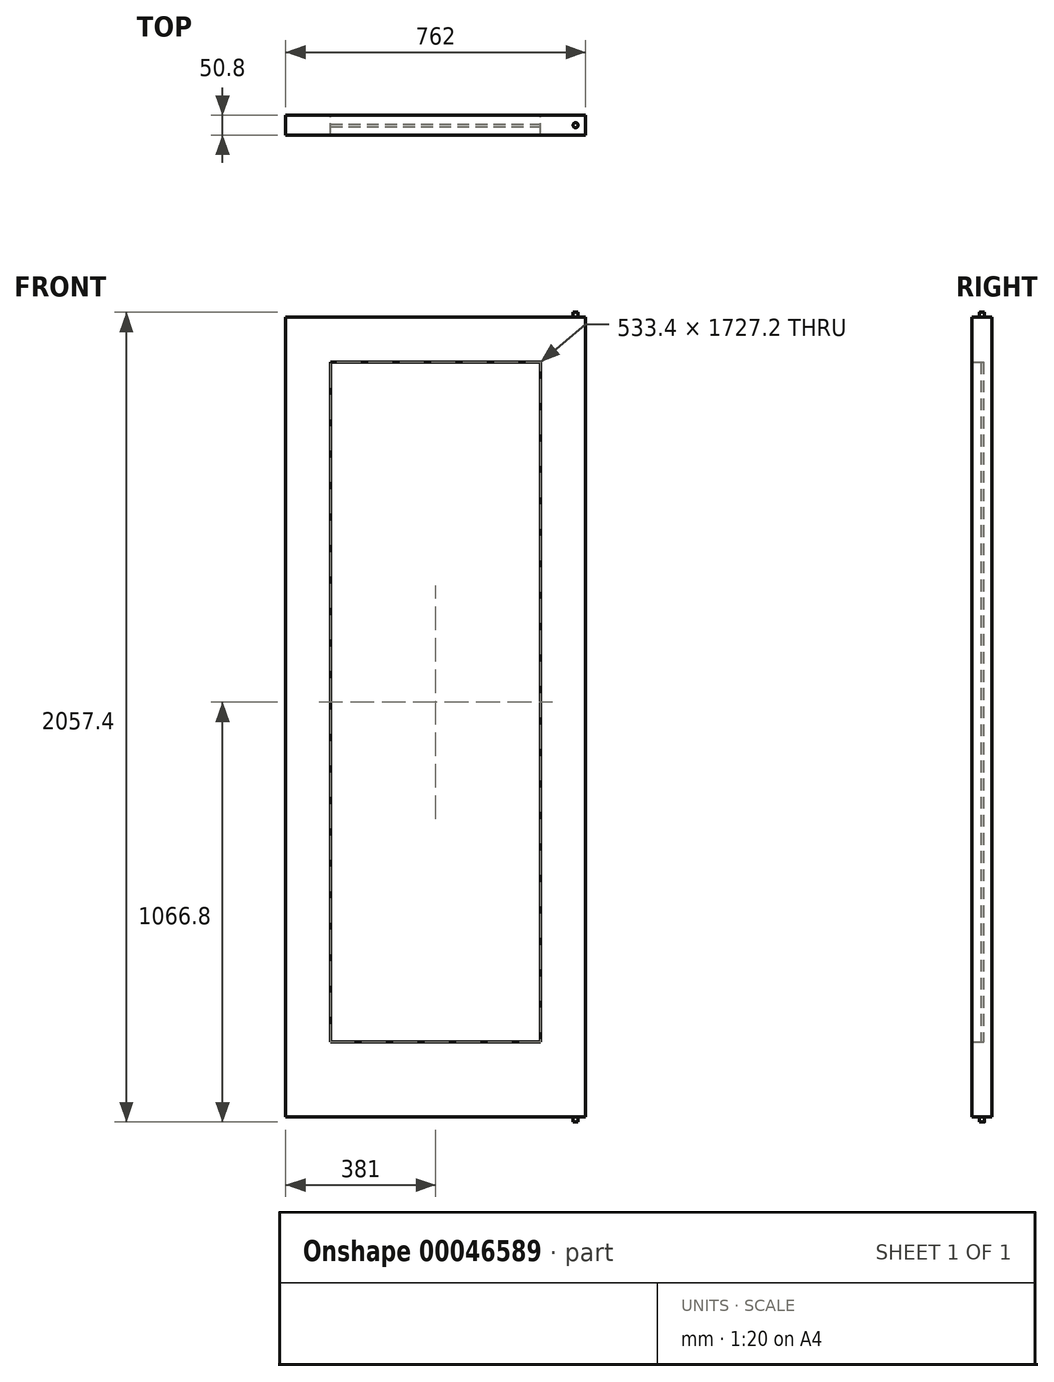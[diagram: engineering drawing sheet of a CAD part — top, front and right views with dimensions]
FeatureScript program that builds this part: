
annotation { "Feature Type Name" : "Feature", "Feature Type Description" : "" }
export const myFeature = defineFeature(function(context is Context, id is Id, definition is map)
    precondition{}
    {
        {
            var Q0;
            Q0=qCreatedBy(makeId("Front.planeOp"),FACE);
            var sketch = newSketch(context, id + "F0", { "sketchPlane" : qUnion([Q0])});
            skLineSegment(sketch, "E0.rect.bottom", {"start": v(381, 1016) * mm, "end": v(-381, 1016) * mm});
            skLineSegment(sketch, "E0.rect.top", {"start": v(381, -1016) * mm, "end": v(-381, -1016) * mm});
            skLineSegment(sketch, "E0.rect.left", {"start": v(381, 1016) * mm, "end": v(381, -1016) * mm});
            skLineSegment(sketch, "E0.rect.right", {"start": v(-381, 1016) * mm, "end": v(-381, -1016) * mm});
            skPoint(sketch, "E0.rect.middle", {"position": v(0, 0) * mm});
            skLineSegment(sketch, "E1.bottom", {"start": v(-266.7, 901.7) * mm, "end": v(266.7, 901.7) * mm});
            skLineSegment(sketch, "E1.top", {"start": v(-266.7, -825.5) * mm, "end": v(266.7, -825.5) * mm});
            skLineSegment(sketch, "E1.left", {"start": v(-266.7, 901.7) * mm, "end": v(-266.7, -825.5) * mm});
            skLineSegment(sketch, "E1.right", {"start": v(266.7, 901.7) * mm, "end": v(266.7, -825.5) * mm});
            skSolve(sketch);
        }
        {
            var Q0;
            Q0=makeQuery(id+"F0.imprint","IMPRINT",FACE,{"disambiguationData":[TD([[makeQuery(id+"F0.imprint","IMPRINT",EDGE,{"derivedFrom":sQuery(id+"F0.wireOp",EDGE,"E0.rect.bottom")}),1.0]])]});
            extrude(context, id + "F1", {"entities" : qUnion([Q0]), "depth" : 25.4 * mm, "hasSecondDirection" : true, "secondDirectionOppositeDirection" : true, "secondDirectionDepth" : 25.4 * mm});
        }
        {
            var Q0;
            Q0=makeQuery(id+"F0.imprint","IMPRINT",FACE,{"disambiguationData":[TD([[makeQuery(id+"F0.imprint","IMPRINT",EDGE,{"derivedFrom":sQuery(id+"F0.wireOp",EDGE,"E1.bottom")}),-1.0]])]});
            extrude(context, id + "F2", {"entities" : qUnion([Q0]), "depth" : 3.17 * mm, "hasSecondDirection" : true, "secondDirectionOppositeDirection" : true, "secondDirectionDepth" : 3.17 * mm});
        }
        {
            var Q0;
            Q0=makeQuery(id+"F1.opExtrude","SWEPT_FACE",FACE,{"disambiguationData":[OSD([sQuery(id+"F0.wireOp",EDGE,"E0.rect.bottom")])]});
            var sketch = newSketch(context, id + "F3", { "sketchPlane" : qUnion([Q0])});
            skLineSegment(sketch, "E2", {"start": v(381, 0) * mm, "end": v(355.6, 0) * mm, "construction": true});
            skCircle(sketch, "E3", {"center": v(355.6, 0) * mm, "radius": 6.35 * mm});
            skSolve(sketch);
        }
        {
            var Q0;
            Q0 = qSketchRegion(id + "F3", true);
            extrude(context, id + "F4", {"entities" : qUnion([Q0]), "operationType" : NewBodyOperationType.ADD, "depth" : 12.7 * mm, "hasSecondDirection" : true, "secondDirectionOppositeDirection" : true, "secondDirectionDepth" : 2044.7 * mm});
        }
    });
